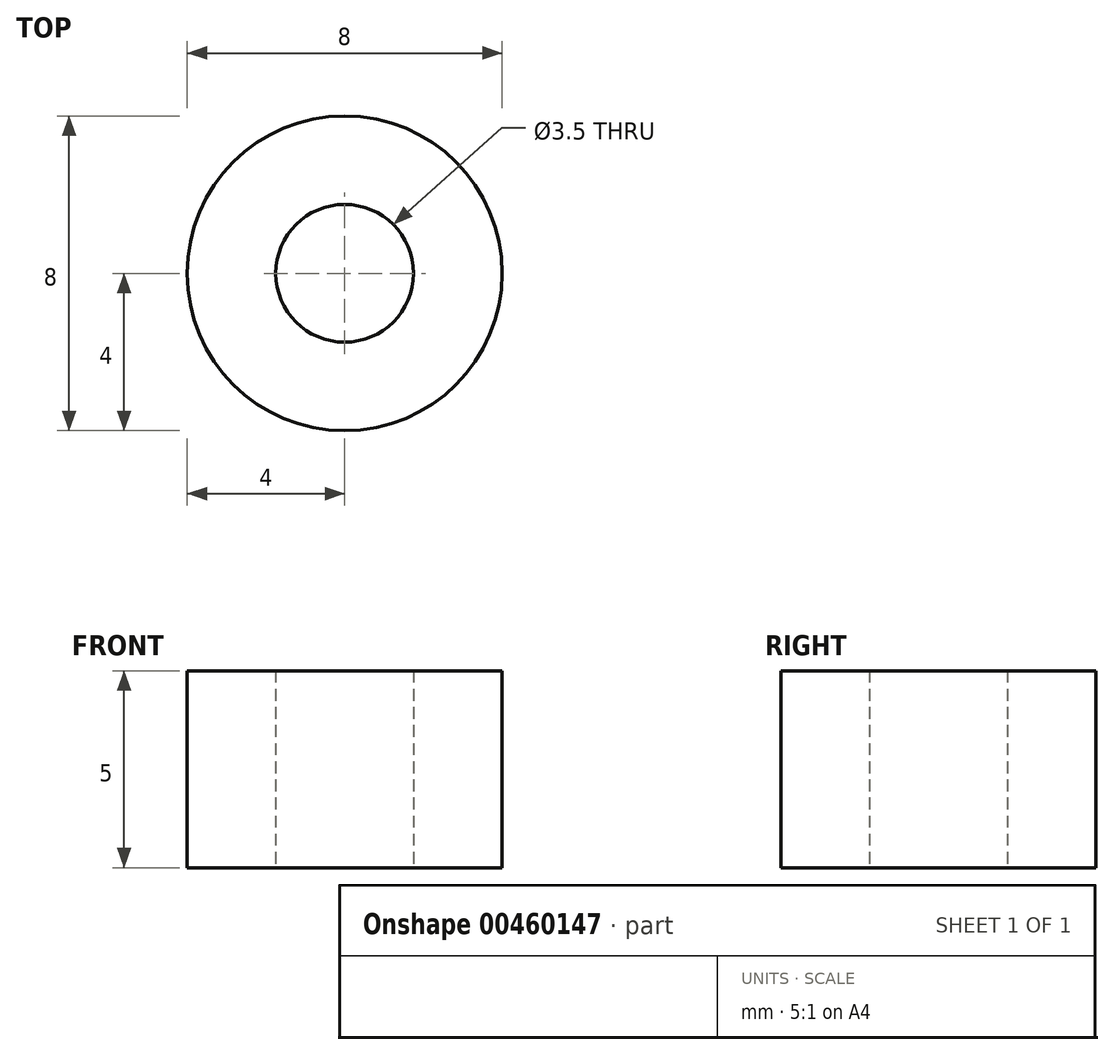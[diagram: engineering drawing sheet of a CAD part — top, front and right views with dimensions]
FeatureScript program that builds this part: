
annotation { "Feature Type Name" : "Feature", "Feature Type Description" : "" }
export const myFeature = defineFeature(function(context is Context, id is Id, definition is map)
    precondition{}
    {
        {
            var Q0;
            Q0=qCreatedBy(makeId("Top.planeOp"),FACE);
            var sketch = newSketch(context, id + "F0", { "sketchPlane" : qUnion([Q0])});
            skCircle(sketch, "E0", {"center": v(0, 0) * mm, "radius": 4 * mm});
            skCircle(sketch, "E1", {"center": v(0, 0) * mm, "radius": 1.75 * mm});
            skSolve(sketch);
        }
        {
            var Q0;
            Q0=makeQuery(id+"F0.imprint","IMPRINT",FACE,{"disambiguationData":[TD([[makeQuery(id+"F0.imprint","IMPRINT",EDGE,{"derivedFrom":sQuery(id+"F0.wireOp",EDGE,"E0")}),1.0]])]});
            extrude(context, id + "F1", {"entities" : qUnion([Q0]), "depth" : 5 * mm});
        }
    });
